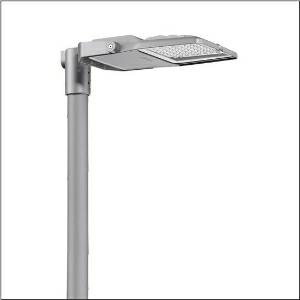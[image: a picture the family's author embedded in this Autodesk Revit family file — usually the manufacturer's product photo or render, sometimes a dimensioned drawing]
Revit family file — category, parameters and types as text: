
# Revit family: floodlight_fl_21_mini___pl33t_5xa7775c2f3a_8bfe
name_source: partatom
category: Lighting Fixtures
units: mm (PartAtom-declared; Revit-internal decimal feet)

## family parameters
Cut with Voids When Loaded = No
Host = Face
Light Source = No
Part Type = Normal
Room Calculation Point = No
Round Connector Dimension = Use Diameter
Shared = No

## types (1)
- --- (1 x LED, 12050 lm, 89 W, 3000K)
    Apparent Load = 89 VA
    CIE Flux Codes = 26 75 99 100 100
    Color Rendering = 70
    Color Temperature = 3000K
    Default Elevation = 1800 mm
    Description = Floodlight FL 21 mini, floodlight, primary light control with lens, of PMMA, primary optical cover: protective disc, of toughened safety glass, transparent, light distribution: PL33T, light emission: direct distribution, installation type: surface-mounted, LED, High Power LED, rated luminous flux: 12.050lm, luminous efficacy: 135lm/W, light colour: 730, colour temperature: 3000K, control gear: Smart Interface (Zhaga), control: flexible luminous flux parameterisation, time-dependent luminous flux control, constant luminous flux control, overheat protection, pre-setting: logarithmic dimming characteristic, with terminal, 6-pole, mains connection: 220..240V, AC, 50/60Hz, start of lifetime: 89W, end of service life: 94W, reduction: 43W, luminaire housing, of diecast aluminium, powder-coated, Siteco® metallic grey (DB 702S), corrosivity category C5 mid according to DIN EN ISO 12944, suitable for swimming pools, chlorine-resistant, sealing non-destructively replaceable, please order mast flange separately, mast bracket, of steel, galvanised, powder-coated, Siteco® metallic grey (DB 702S), Smart Interface above, protection rating (complete): IP66, insulation class (complete): insulation class II (safety insulation), certification: CE, ENEC, VDE, protection symbol: D, impact resistance: IK08, permissible operating ambient temperature: -40..+40°C, permissible operating ambient temperature for outdoor applications: -40..+50°C, standard: DIN EN 12944, LABS conformity tested according to VDMA 24364:2018-05, packaging unit: 1 piece

Light Distribution: PL33T
    Height = 70 mm
    Lamp = 1 x LED
    Lamp Light Flux = 12050 lm
    Lamp Power = 89 W
    Lamp count = 1
    Length = 485 mm
    Luminous efficacy = 135 lm/W
    Manufacturer = Siteco
    ModVariant = No
    Model = 5XA7775C2F3A
    Number of Poles = 1
    OnlyDefault = Yes
    Power Factor = 1
    Product Name = Floodlight FL 21 mini | PL33T
    Product group = floodlight | pylon annexe
    ProductGroupID = 6201
    Protection Class = Protection class II
    Protection Degree = IP 66
    RLX_Detail_Level = 1
    RLX_Emergency_Light_Flux = 0 lm
    RLX_Emergency_Type = 0
    RLX_Emergency_Type_DB = No
    RlxData = <blob elided: 101033 chars, md5=f52130db>
    Socket = socket
    Standby Power = 0 W
    System Light Flux = 12050 lm
    System Power = 89 W
    Type Comments = factory setting: luminous flux: 100 % | dim-lin: 254 | 456 mA
    Type Image = l_1007125.jpg
    URL = http://relux.com
    VarID = @adj_169979
    Voltage = 0 V
    Weight = 0.00 kg
    Width = 337 mm

## geometry (parser evidence)
native form markers: Blend x4, Sweep x11
no freeform markers — native parametric forms only
